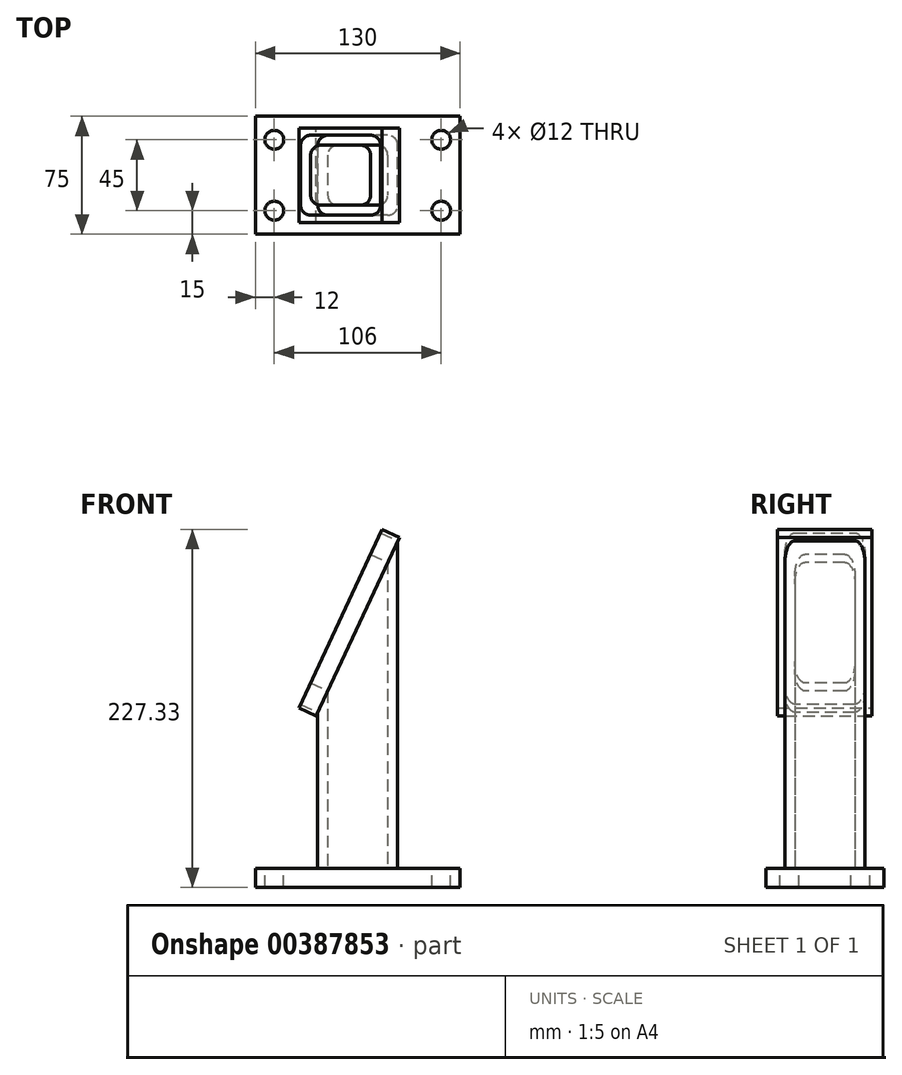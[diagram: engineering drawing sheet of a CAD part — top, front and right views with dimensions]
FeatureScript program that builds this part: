
annotation { "Feature Type Name" : "Feature", "Feature Type Description" : "" }
export const myFeature = defineFeature(function(context is Context, id is Id, definition is map)
    precondition{}
    {
        {
            var Q0;
            Q0=qCreatedBy(makeId("Top.planeOp"),FACE);
            var sketch = newSketch(context, id + "F0", { "sketchPlane" : qUnion([Q0])});
            skLineSegment(sketch, "E0.bottom", {"start": v(65, 37.5) * mm, "end": v(-65, 37.5) * mm});
            skLineSegment(sketch, "E0.top", {"start": v(65, -37.5) * mm, "end": v(-65, -37.5) * mm});
            skLineSegment(sketch, "E0.left", {"start": v(65, 37.5) * mm, "end": v(65, -37.5) * mm});
            skLineSegment(sketch, "E0.right", {"start": v(-65, 37.5) * mm, "end": v(-65, -37.5) * mm});
            skPoint(sketch, "E0.middle", {"position": v(0, 0) * mm});
            skSolve(sketch);
        }
        {
            var Q0;
            Q0=makeQuery(id+"F0.imprint","IMPRINT",FACE,{"disambiguationData":[TD([[makeQuery(id+"F0.imprint","IMPRINT",EDGE,{"derivedFrom":sQuery(id+"F0.wireOp",EDGE,"E0.bottom")}),1.0]])]});
            extrude(context, id + "F1", {"entities" : qUnion([Q0]), "depth" : -12 * mm});
        }
        {
            var Q0;
            Q0=makeQuery(id+"F1.opExtrude","CAP_FACE",FACE,{"disambiguationData":[OSD([sQuery(id+"F0.wireOp",EDGE,"E0.bottom"),sQuery(id+"F0.wireOp",EDGE,"E0.top"),sQuery(id+"F0.wireOp",EDGE,"E0.left"),sQuery(id+"F0.wireOp",EDGE,"E0.right")])],"isStart":true});
            var sketch = newSketch(context, id + "F2", { "sketchPlane" : qUnion([Q0])});
            skLineSegment(sketch, "E1.bottom", {"start": v(19.05, -25.4) * mm, "end": v(-19.05, -25.4) * mm});
            skLineSegment(sketch, "E1.top", {"start": v(19.05, 25.4) * mm, "end": v(-19.05, 25.4) * mm});
            skLineSegment(sketch, "E1.left", {"start": v(25.4, -19.05) * mm, "end": v(25.4, 19.05) * mm});
            skLineSegment(sketch, "E1.right", {"start": v(-25.4, -19.05) * mm, "end": v(-25.4, 19.05) * mm});
            skPoint(sketch, "E1.middle", {"position": v(0, 0) * mm});
            skPoint(sketch, "E2.visualSharp", {"position": v(-25.4, -25.4) * mm});
            skArc(sketch, "E2.filletArc", {"start": v(-25.4, -19.05) * mm, "mid": v(-23.54, -23.54) * mm, "end": v(-19.05, -25.4) * mm});
            skPoint(sketch, "E3.visualSharp", {"position": v(-25.4, 25.4) * mm});
            skArc(sketch, "E3.filletArc", {"start": v(-19.05, 25.4) * mm, "mid": v(-23.54, 23.54) * mm, "end": v(-25.4, 19.05) * mm});
            skPoint(sketch, "E4.visualSharp", {"position": v(25.4, 25.4) * mm});
            skArc(sketch, "E4.filletArc", {"start": v(25.4, 19.05) * mm, "mid": v(23.54, 23.54) * mm, "end": v(19.05, 25.4) * mm});
            skPoint(sketch, "E5.visualSharp", {"position": v(25.4, -25.4) * mm});
            skArc(sketch, "E5.filletArc", {"start": v(19.05, -25.4) * mm, "mid": v(23.54, -23.54) * mm, "end": v(25.4, -19.05) * mm});
            skLineSegment(sketch, "E6.bottom", {"start": v(12.7, 19.05) * mm, "end": v(-12.7, 19.05) * mm});
            skLineSegment(sketch, "E6.top", {"start": v(12.7, -19.05) * mm, "end": v(-12.7, -19.05) * mm});
            skLineSegment(sketch, "E6.left", {"start": v(19.05, 12.7) * mm, "end": v(19.05, -12.7) * mm});
            skLineSegment(sketch, "E6.right", {"start": v(-19.05, 12.7) * mm, "end": v(-19.05, -12.7) * mm});
            skArc(sketch, "E7.filletArc", {"start": v(-12.7, 19.05) * mm, "mid": v(-17.2, 17.2) * mm, "end": v(-19.05, 12.7) * mm});
            skArc(sketch, "E8.filletArc", {"start": v(19.05, 12.7) * mm, "mid": v(17.2, 17.2) * mm, "end": v(12.7, 19.05) * mm});
            skArc(sketch, "E9.filletArc", {"start": v(12.7, -19.05) * mm, "mid": v(17.2, -17.2) * mm, "end": v(19.05, -12.7) * mm});
            skArc(sketch, "E10.filletArc", {"start": v(-19.05, -12.7) * mm, "mid": v(-17.2, -17.2) * mm, "end": v(-12.7, -19.05) * mm});
            skSolve(sketch);
        }
        {
            var Q0;
            Q0=qSketchRegion(id+"F2",true);
            extrude(context, id + "F3", {"entities" : qUnion([Q0]), "operationType" : NewBodyOperationType.ADD, "depth" : (250 - 41.92) * mm});
        }
        {
            var Q0;
            {var subQ0=sQuery(id+"F0.wireOp",EDGE,"E0.left");var subQ1=sQuery(id+"F0.wireOp",EDGE,"E0.bottom");var subQ2=sQuery(id+"F0.wireOp",EDGE,"E0.right");var subQ3=sQuery(id+"F0.wireOp",EDGE,"E0.top");Q0=makeQuery(id+"F3.boolean.opBoolean","SPLIT",FACE,{"disambiguationData":[TD([makeQuery(id+"F1.opExtrude","SWEPT_FACE",FACE,{"disambiguationData":[OSD([subQ1])]})])],"derivedFrom":makeQuery(id+"F1.opExtrude","CAP_FACE",FACE,{"disambiguationData":[OSD([subQ1,subQ3,subQ0,subQ2])],"isStart":true})});}
            var sketch = newSketch(context, id + "F4", { "sketchPlane" : qUnion([Q0])});
            skLineSegment(sketch, "E11", {"start": v(-65, -37.5) * mm, "end": v(-53, -37.5) * mm, "construction": true});
            skLineSegment(sketch, "E12", {"start": v(-53, -37.5) * mm, "end": v(-53, -22.5) * mm, "construction": true});
            skLineSegment(sketch, "E13", {"start": v(-65, 37.5) * mm, "end": v(-53, 37.5) * mm, "construction": true});
            skLineSegment(sketch, "E14", {"start": v(-53, 37.5) * mm, "end": v(-53, 22.5) * mm, "construction": true});
            skLineSegment(sketch, "E15", {"start": v(65, 37.5) * mm, "end": v(53, 37.5) * mm, "construction": true});
            skLineSegment(sketch, "E16", {"start": v(65, -37.5) * mm, "end": v(53, -37.5) * mm, "construction": true});
            skLineSegment(sketch, "E17", {"start": v(53, -37.5) * mm, "end": v(53, -22.5) * mm, "construction": true});
            skLineSegment(sketch, "E18", {"start": v(53, 37.5) * mm, "end": v(53, 22.5) * mm, "construction": true});
            skSolve(sketch);
        }
        {
            var Q0;
            Q0=sQuery(id+"F4.wireOp",VERTEX,"E14.end");
            var Q1;
            Q1=sQuery(id+"F4.wireOp",VERTEX,"E18.end");
            var Q2;
            Q2=sQuery(id+"F4.wireOp",VERTEX,"E17.end");
            var Q3;
            Q3=sQuery(id+"F4.wireOp",VERTEX,"E12.end");
            var Q4;
            Q4=makeQuery(id+"F1.opExtrude","SWEPT_BODY",BODY,{"disambiguationData":[OSD([sQuery(id+"F0.wireOp",EDGE,"E0.bottom"),sQuery(id+"F0.wireOp",EDGE,"E0.top"),sQuery(id+"F0.wireOp",EDGE,"E0.left"),sQuery(id+"F0.wireOp",EDGE,"E0.right")])]});
            hole(context, id + "F5", {"style" : HoleStyle.SIMPLE, "endStyle" : HoleEndStyle.THROUGH, "holeDiameter" : 12 * mm, "isTappedThrough" : true, "tappedDepth" : 12 * mm, "tapClearance" : 3, "locations" : qUnion([Q0, Q1, Q2, Q3]), "scope" : qUnion([Q4])});
        }
        {
            var Q0;
            Q0=makeQuery(id+"F3.opExtrude","SWEPT_FACE",FACE,{"disambiguationData":[OSD([sQuery(id+"F2.wireOp",EDGE,"E1.bottom")])]});
            var sketch = newSketch(context, id + "F6", { "sketchPlane" : qUnion([Q0])});
            skLineSegment(sketch, "E19", {"start": v(-19.05, 208.08) * mm, "end": v(-25.4, 208.08) * mm});
            skLineSegment(sketch, "E20", {"start": v(-25.4, 208.08) * mm, "end": v(25.4, 208.08) * mm});
            skLineSegment(sketch, "E21", {"start": v(25.4, 208.08) * mm, "end": v(-25.4, 99.14) * mm});
            skLineSegment(sketch, "E22", {"start": v(-25.4, 208.08) * mm, "end": v(-25.4, 99.14) * mm});
            skSolve(sketch);
        }
        {
            var Q0;
            {var subQ0=sQuery(id+"F6.wireOp",EDGE,"E20");var subQ1=sQuery(id+"F2.wireOp",EDGE,"E1.bottom");var subQ2=makeQuery(id+"F3.opExtrude","SWEPT_EDGE",EDGE,{"disambiguationData":[OSD([subQ1,sQuery(id+"F2.wireOp",EDGE,"E5.filletArc")])]});var subQ3=makeQuery(id+"F6.imprint","INTERSECT",VERTEX,{"derivedFrom":[subQ2,subQ0]});var subQ4=makeQuery(id+"F3.opExtrude","SWEPT_EDGE",EDGE,{"disambiguationData":[OSD([subQ1,sQuery(id+"F2.wireOp",EDGE,"E2.filletArc")])]});var subQ5=makeQuery(id+"F6.imprint","INTERSECT",VERTEX,{"derivedFrom":[subQ4,subQ0]});Q0=makeQuery(id+"F6.imprint","IMPRINT",FACE,{"disambiguationData":[TD([[makeQuery(id+"F6.imprint","IMPRINT",EDGE,{"disambiguationData":[TD([[subQ3,-1.0],[subQ5,1.0]])],"derivedFrom":subQ0}),1.0]])]});}
            var Q1;
            {var subQ0=sQuery(id+"F6.wireOp",EDGE,"E20");var subQ1=makeQuery(id+"F3.opExtrude","SWEPT_EDGE",EDGE,{"disambiguationData":[OSD([sQuery(id+"F2.wireOp",EDGE,"E1.bottom"),sQuery(id+"F2.wireOp",EDGE,"E5.filletArc")])]});var subQ2=makeQuery(id+"F6.imprint","INTERSECT",VERTEX,{"derivedFrom":[subQ1,subQ0]});var subQ3=sQuery(id+"F6.wireOp",EDGE,"E21");var subQ4=makeQuery(id+"F6.imprint","INTERSECT",VERTEX,{"derivedFrom":[subQ0,subQ3]});Q1=makeQuery(id+"F6.imprint","IMPRINT",FACE,{"disambiguationData":[TD([[makeQuery(id+"F6.imprint","IMPRINT",EDGE,{"disambiguationData":[TD([[subQ2,-1.0],[subQ4,1.0]])],"derivedFrom":subQ0}),-1.0]])]});}
            var Q2;
            {var subQ3=sQuery(id+"F6.wireOp",EDGE,"E22");Q2=makeQuery(id+"F6.imprint","IMPRINT",FACE,{"disambiguationData":[TD([[makeQuery(id+"F6.imprint","IMPRINT",EDGE,{"derivedFrom":subQ3}),1.0]])]});}
            extrude(context, id + "F7", {"entities" : qUnion([Q0, Q1, Q2]), "operationType" : NewBodyOperationType.REMOVE, "oppositeDirection" : true, "depth" : 50.8 * mm});
        }
        {
            var Q0;
            Q0=makeQuery(id+"F7.boolean.opBoolean","COPY",FACE,{"derivedFrom":makeQuery(id+"F7.opExtrude","SWEPT_FACE",FACE,{"disambiguationData":[OSD([sQuery(id+"F6.wireOp",EDGE,"E21")])]})});
            var sketch = newSketch(context, id + "F8", { "sketchPlane" : qUnion([Q0])});
            skLineSegment(sketch, "E23.bottom", {"start": v(30, 201.72) * mm, "end": v(-30, 201.72) * mm});
            skLineSegment(sketch, "E23.top", {"start": v(30, 76.72) * mm, "end": v(-30, 76.72) * mm});
            skLineSegment(sketch, "E23.right", {"start": v(-30, 201.72) * mm, "end": v(-30, 76.72) * mm});
            skPoint(sketch, "E23.middle", {"position": v(0, 139.22) * mm});
            skPoint(sketch, "E23.middle.positionSnap0", {"position": v(-19.05, 139.22) * mm});
            skPoint(sketch, "E23.centerSnap0", {"position": v(-19.05, 139.22) * mm});
            skLineSegment(sketch, "E24", {"start": v(30, 201.72) * mm, "end": v(30, 76.72) * mm});
            skSolve(sketch);
        }
        {
            var Q0;
            Q0=makeQuery(id+"F8.imprint","IMPRINT",FACE,{"disambiguationData":[TD([[makeQuery(id+"F8.imprint","IMPRINT",EDGE,{"derivedFrom":sQuery(id+"F8.wireOp",EDGE,"E23.bottom")}),1.0]])]});
            var Q1;
            {var subQ0=sQuery(id+"F6.wireOp",EDGE,"E21");Q1=makeQuery(id+"F8.imprint","IMPRINT",FACE,{"disambiguationData":[TD([[makeQuery(id+"F8.imprint","IMPRINT",EDGE,{"derivedFrom":makeQuery(id+"F7.boolean.opBoolean","COPY",EDGE,{"derivedFrom":makeQuery(id+"F7.opExtrude","CAP_EDGE",EDGE,{"disambiguationData":[OSD([subQ0])],"isStart":true})})}),-1.0]])]});}
            var Q2;
            {var subQ0=makeQuery(id+"F7.opExtrude","SWEPT_FACE",FACE,{"disambiguationData":[OSD([sQuery(id+"F6.wireOp",EDGE,"E21")])]});Q2=makeQuery(id+"F8.imprint","IMPRINT",FACE,{"disambiguationData":[TD([[makeQuery(id+"F8.imprint","IMPRINT",EDGE,{"derivedFrom":makeQuery(id+"F7.boolean.opBoolean","INTERSECT",EDGE,{"derivedFrom":[makeQuery(id+"F3.opExtrude","SWEPT_FACE",FACE,{"disambiguationData":[OSD([sQuery(id+"F2.wireOp",EDGE,"E6.bottom")])]}),subQ0]})}),1.0]])]});}
            extrude(context, id + "F9", {"entities" : qUnion([Q0, Q1, Q2]), "operationType" : NewBodyOperationType.ADD, "depth" : 12 * mm});
        }
    });
